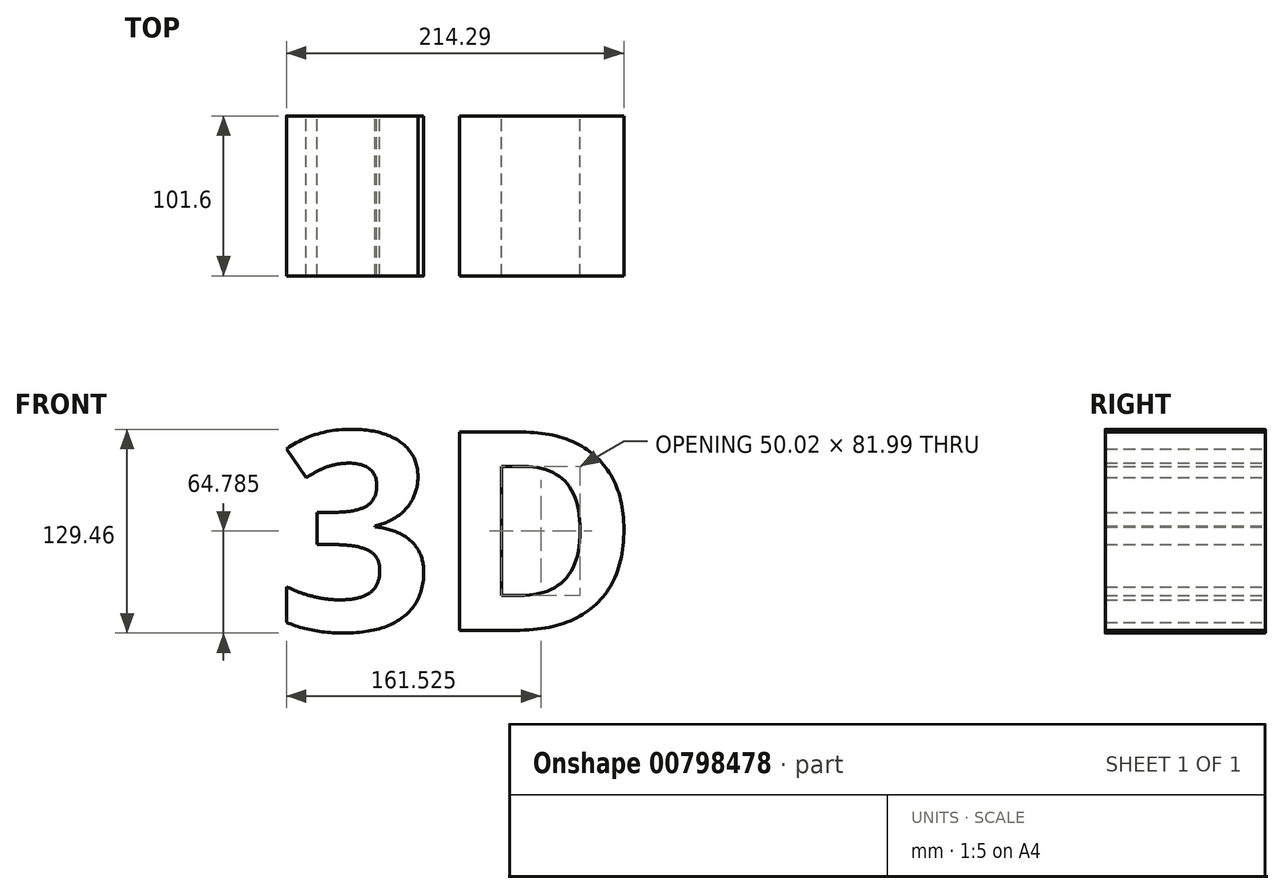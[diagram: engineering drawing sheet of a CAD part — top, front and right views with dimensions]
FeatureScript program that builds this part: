
annotation { "Feature Type Name" : "Feature", "Feature Type Description" : "" }
export const myFeature = defineFeature(function(context is Context, id is Id, definition is map)
    precondition{}
    {
        {
            var Q0;
            Q0=qCreatedBy(makeId("Front.planeOp"),FACE);
            var sketch = newSketch(context, id + "F0", { "sketchPlane" : qUnion([Q0])});
            skLineSegment(sketch, "E0", {"start": v(0, 0) * mm, "end": v(0, 127) * mm});
            skText(sketch, "E1", { "text": "3D", "fontName": "OpenSans-Bold.ttf"});
            const initialGuessF0  = {"E1": [0, 0, 1, 0, 0.127]};
            skSetInitialGuess(sketch, initialGuessF0);
            skSolve(sketch);
        }
        {
            var Q0;
            Q0 = qSketchRegion(id + "F0", true);
            extrude(context, id + "F1", {"entities" : qUnion([Q0]), "depth" : 101.6 * mm, "offsetDistance" : 25.4 * mm});
        }
    });
